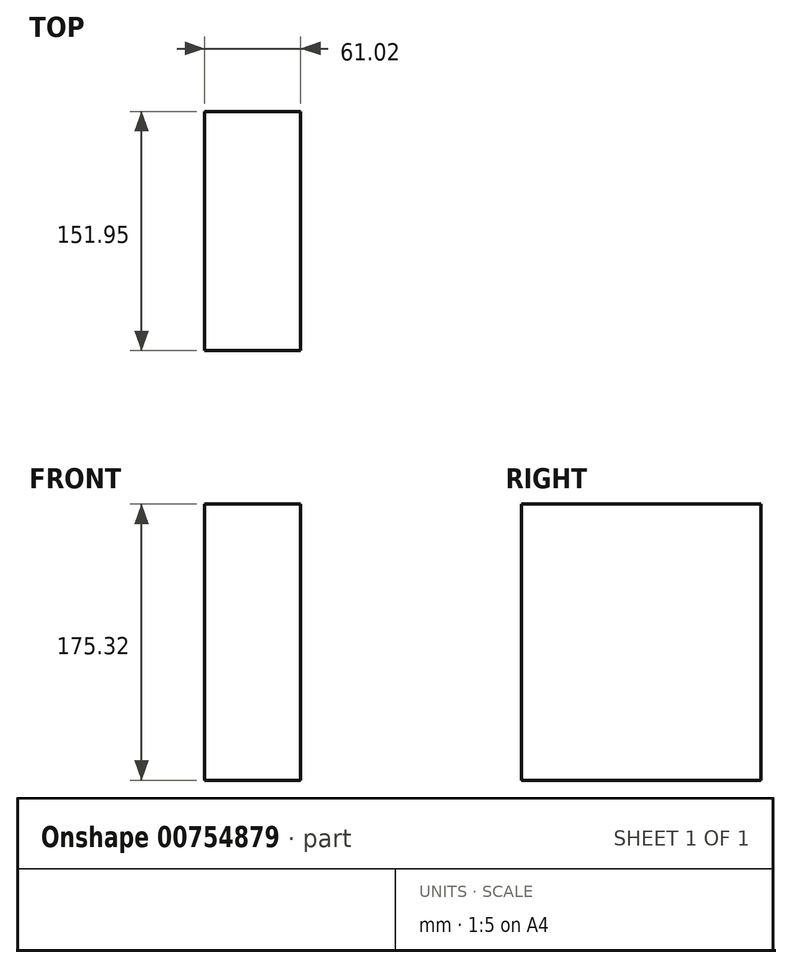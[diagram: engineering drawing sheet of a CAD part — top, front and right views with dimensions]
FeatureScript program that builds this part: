
annotation { "Feature Type Name" : "Feature", "Feature Type Description" : "" }
export const myFeature = defineFeature(function(context is Context, id is Id, definition is map)
    precondition{}
    {
        {
            var Q0;
            Q0=qCreatedBy(makeId("Front.planeOp"),FACE);
            var sketch = newSketch(context, id + "F0", { "sketchPlane" : qUnion([Q0])});
            skLineSegment(sketch, "E0.bottom", {"start": v(0, 17.03) * mm, "end": v(61.02, 17.03) * mm});
            skLineSegment(sketch, "E0.top", {"start": v(0, 112.26) * mm, "end": v(61.02, 112.26) * mm});
            skLineSegment(sketch, "E0.left", {"start": v(0, 17.03) * mm, "end": v(0, 112.26) * mm});
            skLineSegment(sketch, "E0.right", {"start": v(61.02, 17.03) * mm, "end": v(61.02, 112.26) * mm});
            skLineSegment(sketch, "E1.bottom", {"start": v(61.02, 17.03) * mm, "end": v(0, 17.03) * mm});
            skLineSegment(sketch, "E1.top", {"start": v(61.02, -63.06) * mm, "end": v(0, -63.06) * mm});
            skLineSegment(sketch, "E1.left", {"start": v(61.02, 17.03) * mm, "end": v(61.02, -63.06) * mm});
            skLineSegment(sketch, "E1.right", {"start": v(0, 17.03) * mm, "end": v(0, -63.06) * mm});
            skSolve(sketch);
        }
        {
            var Q0;
            Q0 = qSketchRegion(id + "F0", true);
            extrude(context, id + "F1", {"entities" : qUnion([Q0]), "depth" : 151.95 * mm, "offsetDistance" : 25.4 * mm});
        }
    });
